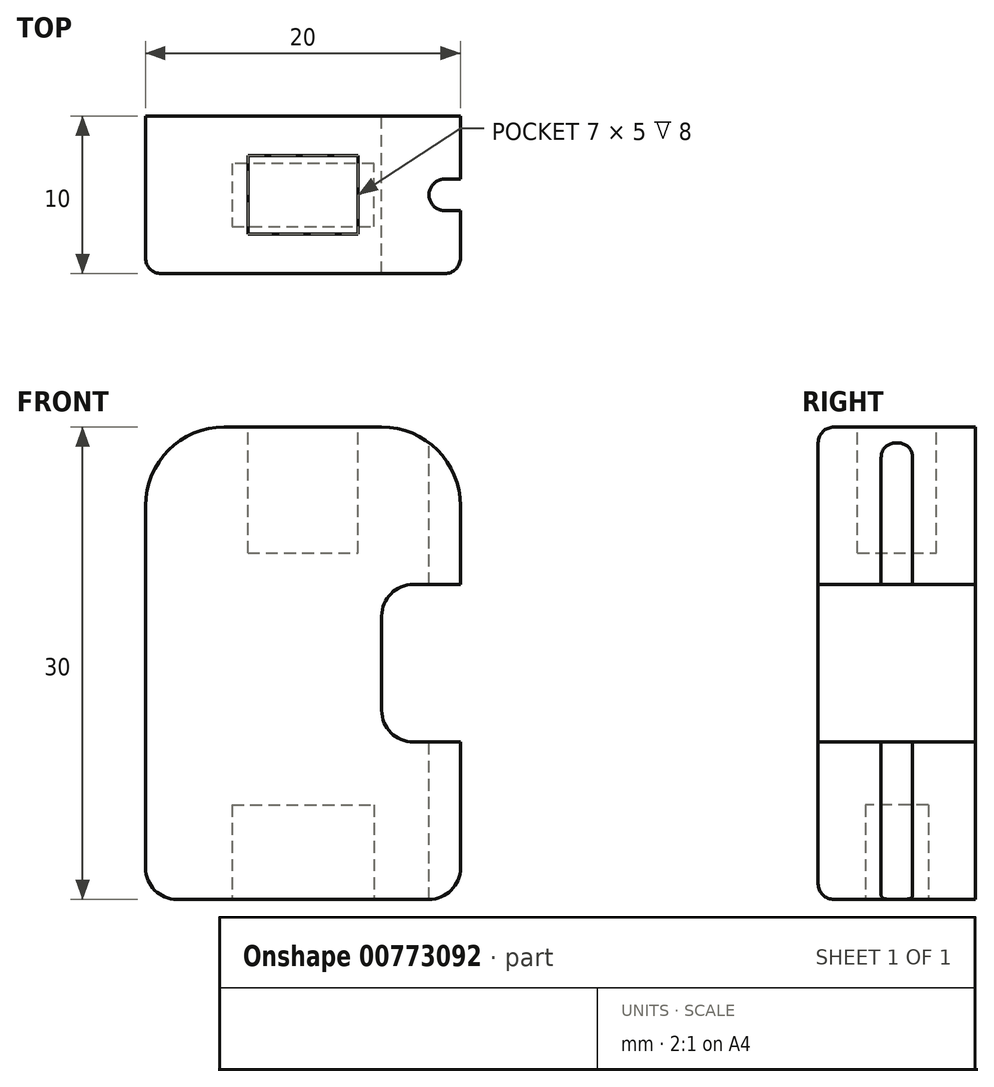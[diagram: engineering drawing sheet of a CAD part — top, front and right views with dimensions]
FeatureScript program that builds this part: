
annotation { "Feature Type Name" : "Feature", "Feature Type Description" : "" }
export const myFeature = defineFeature(function(context is Context, id is Id, definition is map)
    precondition{}
    {
        {
            var Q0;
            Q0=qCreatedBy(makeId("Front.planeOp"),FACE);
            var sketch = newSketch(context, id + "F0", { "sketchPlane" : qUnion([Q0])});
            skLineSegment(sketch, "E0", {"start": v(-2, 0) * mm, "end": v(-18, 0) * mm});
            skLineSegment(sketch, "E1", {"start": v(-20, 2) * mm, "end": v(-20, 25) * mm});
            skLineSegment(sketch, "E2", {"start": v(-15, 30) * mm, "end": v(-5, 30) * mm});
            skLineSegment(sketch, "E3", {"start": v(0, 25) * mm, "end": v(0, 20) * mm});
            skLineSegment(sketch, "E4", {"start": v(0, 20) * mm, "end": v(-5, 20) * mm});
            skLineSegment(sketch, "E5", {"start": v(-5, 20) * mm, "end": v(-5, 10) * mm});
            skLineSegment(sketch, "E6", {"start": v(-5, 10) * mm, "end": v(0, 10) * mm});
            skLineSegment(sketch, "E7", {"start": v(0, 10) * mm, "end": v(0, 2) * mm});
            skPoint(sketch, "E8.visualSharp", {"position": v(0, 30) * mm});
            skArc(sketch, "E8.filletArc", {"start": v(0, 25) * mm, "mid": v(-1.46, 28.54) * mm, "end": v(-5, 30) * mm});
            skPoint(sketch, "E9.visualSharp", {"position": v(0, 0) * mm});
            skArc(sketch, "E9.filletArc", {"start": v(-2, 0) * mm, "mid": v(-0.59, 0.59) * mm, "end": v(0, 2) * mm});
            skPoint(sketch, "E10.visualSharp", {"position": v(-20, 30) * mm});
            skArc(sketch, "E10.filletArc", {"start": v(-15, 30) * mm, "mid": v(-18.54, 28.54) * mm, "end": v(-20, 25) * mm});
            skPoint(sketch, "E11.visualSharp", {"position": v(-20, 0) * mm});
            skArc(sketch, "E11.filletArc", {"start": v(-20, 2) * mm, "mid": v(-19.41, 0.59) * mm, "end": v(-18, 0) * mm});
            skSolve(sketch);
        }
        {
            var Q0;
            Q0=makeQuery(id+"F0.imprint","IMPRINT",FACE,{"disambiguationData":[TD([[makeQuery(id+"F0.imprint","IMPRINT",EDGE,{"derivedFrom":sQuery(id+"F0.wireOp",EDGE,"E0")}),-1.0]])]});
            extrude(context, id + "F1", {"entities" : qUnion([Q0]), "depth" : 10 * mm, "offsetDistance" : 25 * mm});
        }
        {
            var Q0;
            Q0=makeQuery(id+"F1.opExtrude","CAP_EDGE",EDGE,{"disambiguationData":[OSD([sQuery(id+"F0.wireOp",EDGE,"E2")])],"isStart":false});
            fillet(context, id + "F2", {"entities" : qUnion([Q0]), "radius" : 1 * mm, "tangentPropagation" : true, "allowEdgeOverflow" : false});
        }
        {
            var Q0;
            Q0=makeQuery(id+"F1.opExtrude","SWEPT_FACE",FACE,{"disambiguationData":[OSD([sQuery(id+"F0.wireOp",EDGE,"E4")])]});
            var sketch = newSketch(context, id + "F3", { "sketchPlane" : qUnion([Q0])});
            skLineSegment(sketch, "E12", {"start": v(0, 6) * mm, "end": v(-2, 6) * mm});
            skLineSegment(sketch, "E13", {"start": v(-2, 6) * mm, "end": v(-2, 4) * mm});
            skLineSegment(sketch, "E14", {"start": v(-2, 4) * mm, "end": v(0, 4) * mm});
            skLineSegment(sketch, "E15", {"start": v(0, 4) * mm, "end": v(0, 6) * mm});
            skSolve(sketch);
        }
        {
            var Q0;
            Q0 = qSketchRegion(id + "F3", true);
            extrude(context, id + "F4", {"entities" : qUnion([Q0]), "operationType" : NewBodyOperationType.REMOVE, "endBound" : BoundingType.SYMMETRIC, "oppositeDirection" : true, "depth" : 40 * mm, "offsetDistance" : 25 * mm});
        }
        {
            var Q0;
            Q0=makeQuery(id+"F1.opExtrude","SWEPT_EDGE",EDGE,{"disambiguationData":[OSD([sQuery(id+"F0.wireOp",EDGE,"E4"),sQuery(id+"F0.wireOp",EDGE,"E5")])]});
            fillet(context, id + "F5", {"entities" : qUnion([Q0]), "radius" : 2 * mm, "tangentPropagation" : true, "allowEdgeOverflow" : false});
        }
        {
            var Q0;
            Q0=makeQuery(id+"F1.opExtrude","SWEPT_EDGE",EDGE,{"disambiguationData":[OSD([sQuery(id+"F0.wireOp",EDGE,"E5"),sQuery(id+"F0.wireOp",EDGE,"E6")])]});
            fillet(context, id + "F6", {"entities" : qUnion([Q0]), "radius" : 2 * mm, "tangentPropagation" : true, "allowEdgeOverflow" : false});
        }
        {
            var Q0;
            Q0=makeQuery(id+"F1.opExtrude","SWEPT_FACE",FACE,{"disambiguationData":[OSD([sQuery(id+"F0.wireOp",EDGE,"E2")])]});
            var sketch = newSketch(context, id + "F7", { "sketchPlane" : qUnion([Q0])});
            skLineSegment(sketch, "E16", {"start": v(-13.5, -2.5) * mm, "end": v(-6.5, -2.5) * mm});
            skLineSegment(sketch, "E17", {"start": v(-6.5, -2.5) * mm, "end": v(-6.5, -7.5) * mm});
            skLineSegment(sketch, "E18", {"start": v(-6.5, -7.5) * mm, "end": v(-13.5, -7.5) * mm});
            skLineSegment(sketch, "E19", {"start": v(-13.5, -7.5) * mm, "end": v(-13.5, -2.5) * mm});
            skSolve(sketch);
        }
        {
            var Q0;
            Q0=makeQuery(id+"F7.imprint","IMPRINT",FACE,{"disambiguationData":[TD([[makeQuery(id+"F7.imprint","IMPRINT",EDGE,{"derivedFrom":sQuery(id+"F7.wireOp",EDGE,"E16")}),-1.0]])]});
            extrude(context, id + "F8", {"entities" : qUnion([Q0]), "operationType" : NewBodyOperationType.REMOVE, "oppositeDirection" : true, "depth" : 8 * mm, "offsetDistance" : 25 * mm});
        }
        {
            var Q0;
            {var subQ0=sQuery(id+"F3.wireOp",EDGE,"E13");var subQ1=sQuery(id+"F3.wireOp",EDGE,"E14");Q0=makeQuery(id+"F4.boolean.opBoolean","COPY",EDGE,{"disambiguationData":[TD([makeQuery(id+"F1.opExtrude","SWEPT_FACE",FACE,{"disambiguationData":[OSD([sQuery(id+"F0.wireOp",EDGE,"E4")])]})])],"derivedFrom":makeQuery(id+"F4.opExtrude","SWEPT_EDGE",EDGE,{"disambiguationData":[OSD([subQ0,subQ1])]})});}
            var Q1;
            {var subQ0=sQuery(id+"F3.wireOp",EDGE,"E12");var subQ1=sQuery(id+"F3.wireOp",EDGE,"E13");Q1=makeQuery(id+"F4.boolean.opBoolean","COPY",EDGE,{"disambiguationData":[TD([makeQuery(id+"F1.opExtrude","SWEPT_FACE",FACE,{"disambiguationData":[OSD([sQuery(id+"F0.wireOp",EDGE,"E4")])]})])],"derivedFrom":makeQuery(id+"F4.opExtrude","SWEPT_EDGE",EDGE,{"disambiguationData":[OSD([subQ0,subQ1])]})});}
            var Q2;
            {var subQ0=sQuery(id+"F3.wireOp",EDGE,"E12");var subQ1=sQuery(id+"F3.wireOp",EDGE,"E13");Q2=makeQuery(id+"F4.boolean.opBoolean","COPY",EDGE,{"disambiguationData":[TD([makeQuery(id+"F1.opExtrude","SWEPT_FACE",FACE,{"disambiguationData":[OSD([sQuery(id+"F0.wireOp",EDGE,"E0")])]})])],"derivedFrom":makeQuery(id+"F4.opExtrude","SWEPT_EDGE",EDGE,{"disambiguationData":[OSD([subQ0,subQ1])]})});}
            var Q3;
            {var subQ0=sQuery(id+"F3.wireOp",EDGE,"E13");var subQ1=sQuery(id+"F3.wireOp",EDGE,"E14");Q3=makeQuery(id+"F4.boolean.opBoolean","COPY",EDGE,{"disambiguationData":[TD([makeQuery(id+"F1.opExtrude","SWEPT_FACE",FACE,{"disambiguationData":[OSD([sQuery(id+"F0.wireOp",EDGE,"E0")])]})])],"derivedFrom":makeQuery(id+"F4.opExtrude","SWEPT_EDGE",EDGE,{"disambiguationData":[OSD([subQ0,subQ1])]})});}
            fillet(context, id + "F9", {"entities" : qUnion([Q0, Q1, Q2, Q3]), "radius" : 1 * mm, "tangentPropagation" : true, "allowEdgeOverflow" : false});
        }
        {
            var Q0;
            Q0=makeQuery(id+"F1.opExtrude","SWEPT_FACE",FACE,{"disambiguationData":[OSD([sQuery(id+"F0.wireOp",EDGE,"E0")])]});
            var sketch = newSketch(context, id + "F10", { "sketchPlane" : qUnion([Q0])});
            skLineSegment(sketch, "E20", {"start": v(-14.5, 7) * mm, "end": v(-5.5, 7) * mm});
            skLineSegment(sketch, "E21", {"start": v(-5.5, 7) * mm, "end": v(-5.5, 3) * mm});
            skLineSegment(sketch, "E22", {"start": v(-5.5, 3) * mm, "end": v(-14.5, 3) * mm});
            skLineSegment(sketch, "E23", {"start": v(-14.5, 3) * mm, "end": v(-14.5, 7) * mm});
            skSolve(sketch);
        }
        {
            var Q0;
            Q0 = qSketchRegion(id + "F10", true);
            extrude(context, id + "F11", {"entities" : qUnion([Q0]), "operationType" : NewBodyOperationType.REMOVE, "oppositeDirection" : true, "depth" : 6 * mm, "offsetDistance" : 25 * mm});
        }
    });
